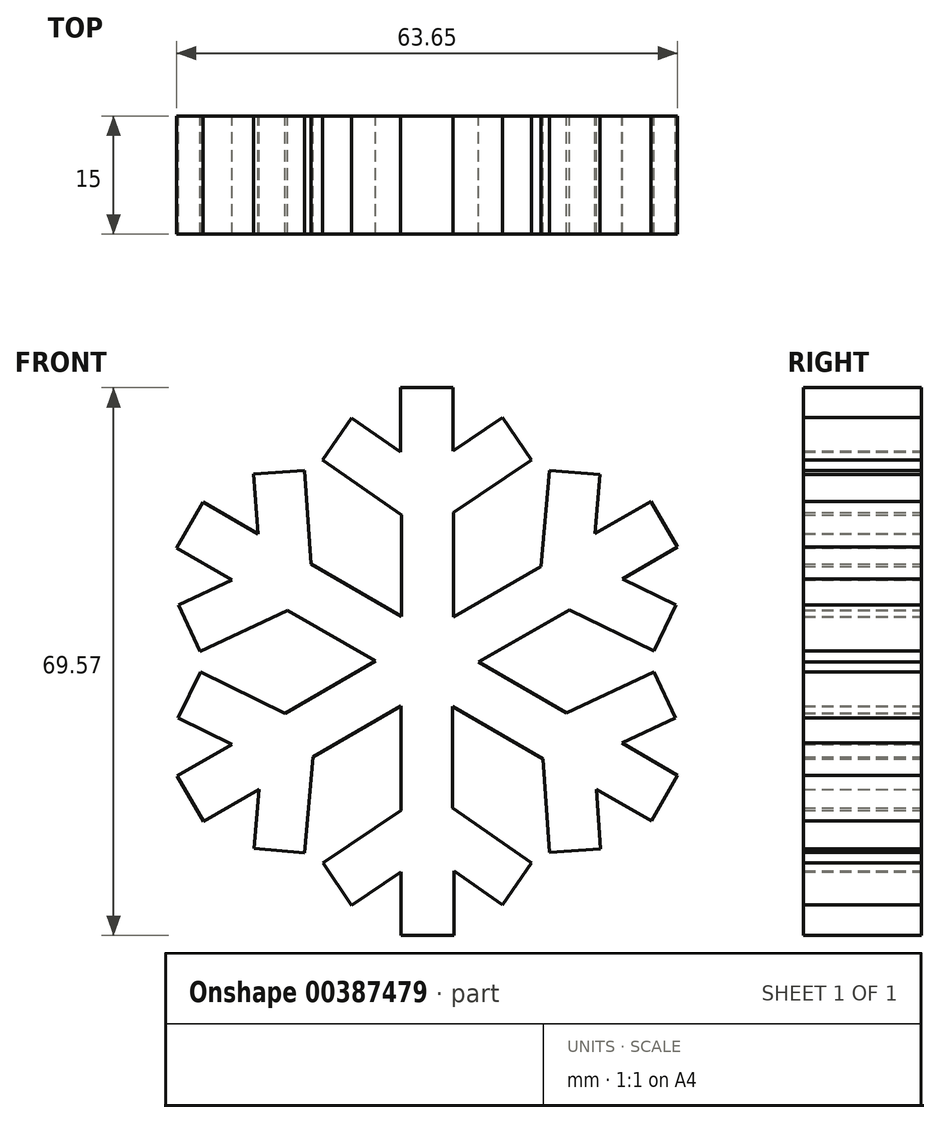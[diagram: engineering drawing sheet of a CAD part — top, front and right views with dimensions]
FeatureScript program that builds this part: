
annotation { "Feature Type Name" : "Feature", "Feature Type Description" : "" }
export const myFeature = defineFeature(function(context is Context, id is Id, definition is map)
    precondition{}
    {
        {
            var Q0;
            Q0=qCreatedBy(makeId("Front.planeOp"),FACE);
            var sketch = newSketch(context, id + "F0", { "sketchPlane" : qUnion([Q0])});
            skLineSegment(sketch, "E0", {"start": v(35.01, 31.88) * mm, "end": v(35.01, 18.4) * mm});
            skLineSegment(sketch, "E1", {"start": v(35.01, 18.4) * mm, "end": v(25.12, 11.73) * mm});
            skLineSegment(sketch, "E2", {"start": v(25.12, 11.73) * mm, "end": v(28.74, 6.36) * mm});
            skLineSegment(sketch, "E3", {"start": v(28.74, 6.36) * mm, "end": v(35.05, 10.6) * mm});
            skLineSegment(sketch, "E4", {"start": v(35.05, 10.6) * mm, "end": v(35.05, 2.55) * mm});
            skLineSegment(sketch, "E5", {"start": v(35.05, 2.55) * mm, "end": v(41.76, 2.55) * mm});
            skLineSegment(sketch, "E6", {"start": v(41.76, 2.55) * mm, "end": v(41.76, 10.73) * mm});
            skLineSegment(sketch, "E7", {"start": v(41.76, 10.73) * mm, "end": v(47.92, 6.43) * mm});
            skLineSegment(sketch, "E8", {"start": v(47.92, 6.43) * mm, "end": v(51.62, 11.73) * mm});
            skLineSegment(sketch, "E9", {"start": v(51.62, 11.73) * mm, "end": v(41.58, 18.74) * mm});
            skLineSegment(sketch, "E10", {"start": v(41.58, 18.74) * mm, "end": v(41.58, 32.03) * mm});
            skLineSegment(sketch, "E11.1.0", {"start": v(56.07, 30.83) * mm, "end": v(44.57, 37.47) * mm});
            skLineSegment(sketch, "E11.1.1", {"start": v(41.4, 31.72) * mm, "end": v(53.08, 24.98) * mm});
            skLineSegment(sketch, "E11.1.2", {"start": v(53.08, 24.98) * mm, "end": v(53.91, 13.07) * mm});
            skLineSegment(sketch, "E11.1.3", {"start": v(53.91, 13.07) * mm, "end": v(60.38, 13.52) * mm});
            skLineSegment(sketch, "E11.1.4", {"start": v(67.16, 36.03) * mm, "end": v(56.07, 30.83) * mm});
            skLineSegment(sketch, "E11.1.5", {"start": v(69.9, 30.17) * mm, "end": v(67.16, 36.03) * mm});
            skLineSegment(sketch, "E11.1.6", {"start": v(63.1, 26.98) * mm, "end": v(69.9, 30.17) * mm});
            skLineSegment(sketch, "E11.1.7", {"start": v(70.18, 22.9) * mm, "end": v(63.1, 26.98) * mm});
            skLineSegment(sketch, "E11.1.8", {"start": v(59.85, 21.11) * mm, "end": v(66.83, 17.08) * mm});
            skLineSegment(sketch, "E11.1.9", {"start": v(60.38, 13.52) * mm, "end": v(59.85, 21.11) * mm});
            skLineSegment(sketch, "E11.1.10", {"start": v(66.83, 17.08) * mm, "end": v(70.18, 22.9) * mm});
            skLineSegment(sketch, "E11.2.0", {"start": v(52.85, 49.43) * mm, "end": v(41.34, 42.79) * mm});
            skLineSegment(sketch, "E11.2.1", {"start": v(44.75, 37.17) * mm, "end": v(56.42, 43.91) * mm});
            skLineSegment(sketch, "E11.2.2", {"start": v(56.42, 43.91) * mm, "end": v(67.15, 38.68) * mm});
            skLineSegment(sketch, "E11.2.3", {"start": v(67.15, 38.68) * mm, "end": v(70, 44.5) * mm});
            skLineSegment(sketch, "E11.2.4", {"start": v(53.9, 61.63) * mm, "end": v(52.85, 49.43) * mm});
            skLineSegment(sketch, "E11.2.5", {"start": v(60.34, 61.08) * mm, "end": v(53.9, 61.63) * mm});
            skLineSegment(sketch, "E11.2.6", {"start": v(59.7, 53.59) * mm, "end": v(60.34, 61.08) * mm});
            skLineSegment(sketch, "E11.2.7", {"start": v(66.78, 57.68) * mm, "end": v(59.7, 53.59) * mm});
            skLineSegment(sketch, "E11.2.8", {"start": v(63.16, 47.84) * mm, "end": v(70.13, 51.87) * mm});
            skLineSegment(sketch, "E11.2.9", {"start": v(70, 44.5) * mm, "end": v(63.16, 47.84) * mm});
            skLineSegment(sketch, "E11.2.10", {"start": v(70.13, 51.87) * mm, "end": v(66.78, 57.68) * mm});
            skLineSegment(sketch, "E11.3.0", {"start": v(35.13, 55.93) * mm, "end": v(35.13, 42.65) * mm});
            skLineSegment(sketch, "E11.3.1", {"start": v(41.7, 42.8) * mm, "end": v(41.7, 56.27) * mm});
            skLineSegment(sketch, "E11.3.2", {"start": v(41.7, 56.27) * mm, "end": v(51.59, 62.94) * mm});
            skLineSegment(sketch, "E11.3.3", {"start": v(51.59, 62.94) * mm, "end": v(47.96, 68.32) * mm});
            skLineSegment(sketch, "E11.3.4", {"start": v(25.08, 62.94) * mm, "end": v(35.13, 55.93) * mm});
            skLineSegment(sketch, "E11.3.5", {"start": v(28.79, 68.25) * mm, "end": v(25.08, 62.94) * mm});
            skLineSegment(sketch, "E11.3.6", {"start": v(34.95, 63.95) * mm, "end": v(28.79, 68.25) * mm});
            skLineSegment(sketch, "E11.3.7", {"start": v(34.95, 72.12) * mm, "end": v(34.95, 63.95) * mm});
            skLineSegment(sketch, "E11.3.8", {"start": v(41.66, 64.07) * mm, "end": v(41.66, 72.12) * mm});
            skLineSegment(sketch, "E11.3.9", {"start": v(47.96, 68.32) * mm, "end": v(41.66, 64.07) * mm});
            skLineSegment(sketch, "E11.3.10", {"start": v(41.66, 72.12) * mm, "end": v(34.95, 72.12) * mm});
            skLineSegment(sketch, "E11.4.0", {"start": v(20.64, 43.84) * mm, "end": v(32.14, 37.2) * mm});
            skLineSegment(sketch, "E11.4.1", {"start": v(35.3, 42.96) * mm, "end": v(23.62, 49.7) * mm});
            skLineSegment(sketch, "E11.4.2", {"start": v(23.62, 49.7) * mm, "end": v(22.8, 61.6) * mm});
            skLineSegment(sketch, "E11.4.3", {"start": v(22.8, 61.6) * mm, "end": v(16.33, 61.15) * mm});
            skLineSegment(sketch, "E11.4.4", {"start": v(9.54, 38.65) * mm, "end": v(20.64, 43.84) * mm});
            skLineSegment(sketch, "E11.4.5", {"start": v(6.8, 44.5) * mm, "end": v(9.54, 38.65) * mm});
            skLineSegment(sketch, "E11.4.6", {"start": v(13.6, 47.7) * mm, "end": v(6.8, 44.5) * mm});
            skLineSegment(sketch, "E11.4.7", {"start": v(6.53, 51.78) * mm, "end": v(13.6, 47.7) * mm});
            skLineSegment(sketch, "E11.4.8", {"start": v(16.86, 53.57) * mm, "end": v(9.88, 57.6) * mm});
            skLineSegment(sketch, "E11.4.9", {"start": v(16.33, 61.15) * mm, "end": v(16.86, 53.57) * mm});
            skLineSegment(sketch, "E11.4.10", {"start": v(9.88, 57.6) * mm, "end": v(6.53, 51.78) * mm});
            skLineSegment(sketch, "E11.5.0", {"start": v(23.86, 25.25) * mm, "end": v(35.37, 31.9) * mm});
            skLineSegment(sketch, "E11.5.1", {"start": v(31.96, 37.5) * mm, "end": v(20.28, 30.76) * mm});
            skLineSegment(sketch, "E11.5.2", {"start": v(20.28, 30.76) * mm, "end": v(9.56, 36) * mm});
            skLineSegment(sketch, "E11.5.3", {"start": v(9.56, 36) * mm, "end": v(6.72, 30.17) * mm});
            skLineSegment(sketch, "E11.5.4", {"start": v(22.81, 13.04) * mm, "end": v(23.86, 25.25) * mm});
            skLineSegment(sketch, "E11.5.5", {"start": v(16.37, 13.6) * mm, "end": v(22.81, 13.04) * mm});
            skLineSegment(sketch, "E11.5.6", {"start": v(17.01, 21.09) * mm, "end": v(16.37, 13.6) * mm});
            skLineSegment(sketch, "E11.5.7", {"start": v(9.93, 17) * mm, "end": v(17.01, 21.09) * mm});
            skLineSegment(sketch, "E11.5.8", {"start": v(13.55, 26.83) * mm, "end": v(6.58, 22.8) * mm});
            skLineSegment(sketch, "E11.5.9", {"start": v(6.72, 30.17) * mm, "end": v(13.55, 26.83) * mm});
            skLineSegment(sketch, "E11.5.10", {"start": v(6.58, 22.8) * mm, "end": v(9.93, 17) * mm});
            skPoint(sketch, "E11.center", {"position": v(38.35, 37.34) * mm});
            skSolve(sketch);
        }
        {
            var Q0;
            {var subQ19=sQuery(id+"F0.wireOp",EDGE,"E1");Q0=makeQuery(id+"F0.imprint","IMPRINT",FACE,{"disambiguationData":[TD([[makeQuery(id+"F0.imprint","IMPRINT",EDGE,{"derivedFrom":subQ19}),1.0]])]});}
            extrude(context, id + "F1", {"entities" : qUnion([Q0]), "depth" : 15 * mm});
        }
    });
